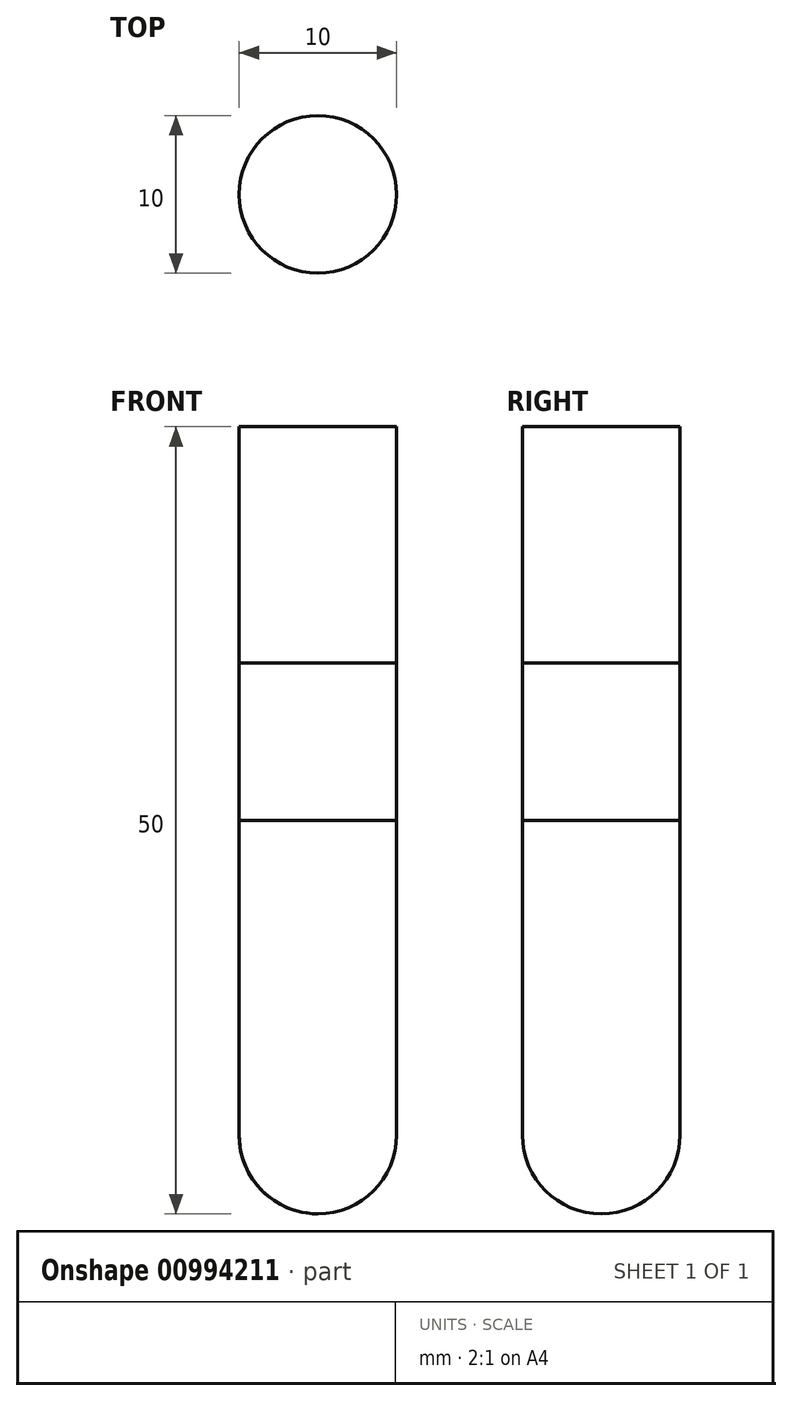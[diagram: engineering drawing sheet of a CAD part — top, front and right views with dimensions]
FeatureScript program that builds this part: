
annotation { "Feature Type Name" : "Feature", "Feature Type Description" : "" }
export const myFeature = defineFeature(function(context is Context, id is Id, definition is map)
    precondition{}
    {
        {
            var Q0;
            Q0=qCreatedBy(makeId("Top.planeOp"),FACE);
            var sketch = newSketch(context, id + "F0", { "sketchPlane" : qUnion([Q0])});
            skCircle(sketch, "E0", {"center": v(0, 0) * mm, "radius": 5 * mm});
            skSolve(sketch);
        }
        {
            var Q0;
            Q0 = qSketchRegion(id + "F0", true);
            extrude(context, id + "F1", {"entities" : qUnion([Q0]), "depth" : 10 * mm, "offsetDistance" : 25 * mm});
        }
        {
            var Q0;
            Q0=makeQuery(id+"F1.opExtrude","CAP_FACE",FACE,{"disambiguationData":[OSD([sQuery(id+"F0.wireOp",EDGE,"E0")])],"isStart":false});
            var sketch = newSketch(context, id + "F2", { "sketchPlane" : qUnion([Q0])});
            skCircle(sketch, "E1", {"center": v(0, 0) * mm, "radius": 5 * mm});
            skSolve(sketch);
        }
        {
            var Q0;
            Q0 = qSketchRegion(id + "F2", true);
            extrude(context, id + "F3", {"entities" : qUnion([Q0]), "depth" : 15 * mm, "offsetDistance" : 25 * mm});
        }
        {
            var Q0;
            Q0=makeQuery(id+"F1.opExtrude","CAP_FACE",FACE,{"disambiguationData":[OSD([sQuery(id+"F0.wireOp",EDGE,"E0")])],"isStart":true});
            var sketch = newSketch(context, id + "F4", { "sketchPlane" : qUnion([Q0])});
            skCircle(sketch, "E2", {"center": v(0, 0) * mm, "radius": 5 * mm});
            skSolve(sketch);
        }
        {
            var Q0;
            Q0 = qSketchRegion(id + "F4", true);
            extrude(context, id + "F5", {"entities" : qUnion([Q0]), "depth" : 25 * mm, "offsetDistance" : 25 * mm});
        }
        {
            var Q0;
            Q0=makeQuery(id+"F5.opExtrude","CAP_EDGE",EDGE,{"disambiguationData":[OSD([sQuery(id+"F4.wireOp",EDGE,"E2")])],"isStart":false});
            fillet(context, id + "F6", {"entities" : qUnion([Q0]), "radius" : 5 * mm, "tangentPropagation" : true, "allowEdgeOverflow" : false});
        }
    });
